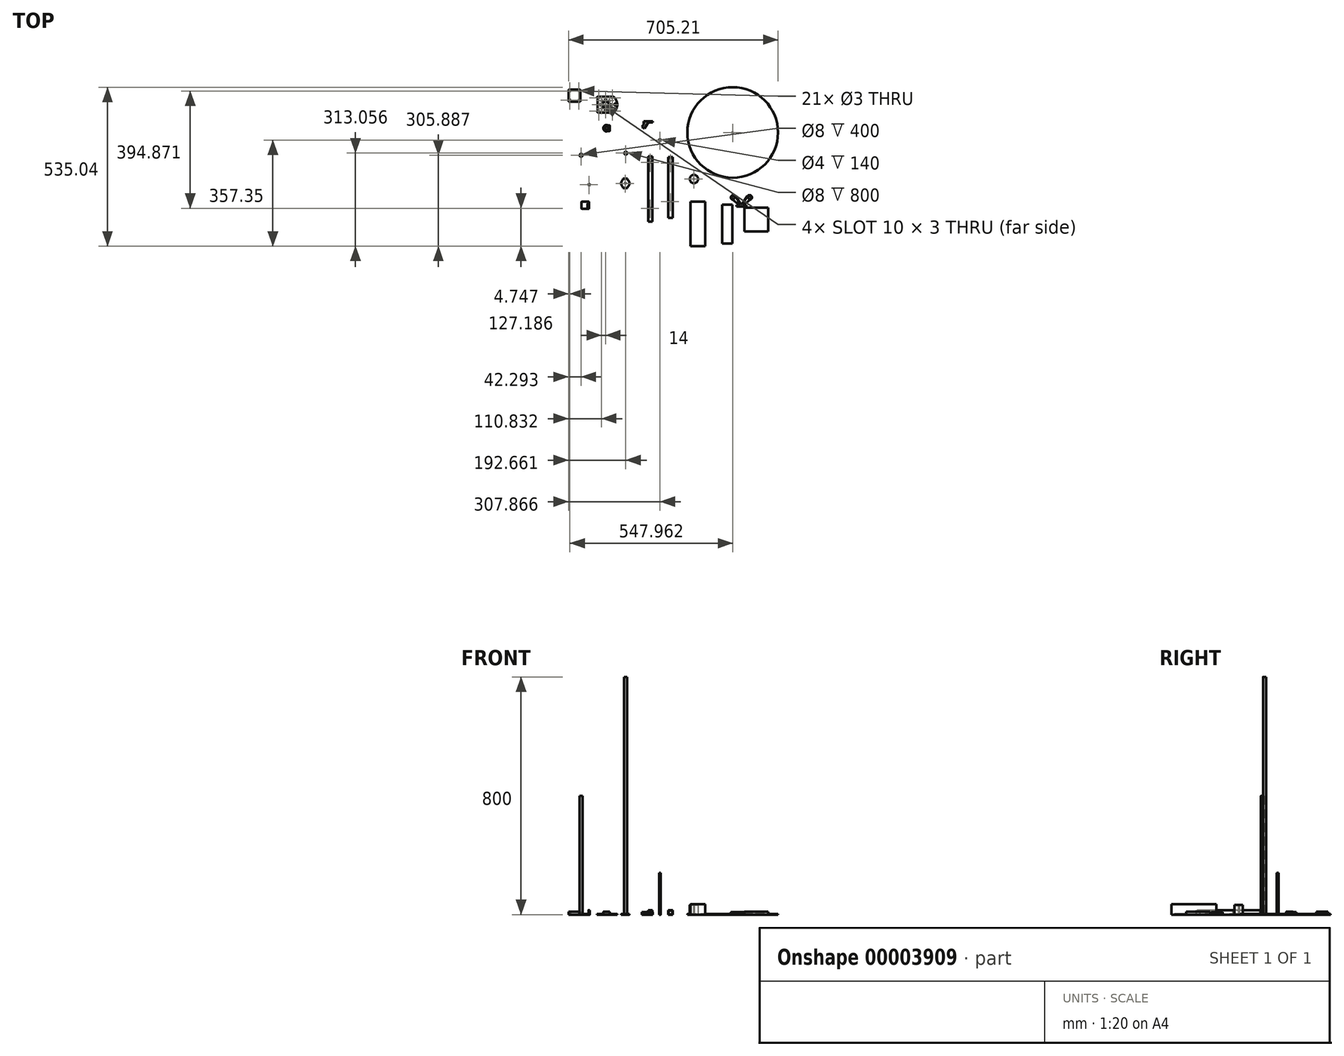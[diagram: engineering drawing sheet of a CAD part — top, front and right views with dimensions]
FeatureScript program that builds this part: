
annotation { "Feature Type Name" : "Feature", "Feature Type Description" : "" }
export const myFeature = defineFeature(function(context is Context, id is Id, definition is map)
    precondition{}
    {
        {
            var Q0;
            Q0=qCreatedBy(makeId("Top.planeOp"),FACE);
            var sketch = newSketch(context, id + "F0", { "sketchPlane" : qUnion([Q0])});
            skLineSegment(sketch, "E0.bottom", {"start": v(-54.12, 60.88) * mm, "end": v(-39.12, 60.88) * mm});
            skLineSegment(sketch, "E0.top", {"start": v(-54.12, -159.12) * mm, "end": v(-39.12, -159.12) * mm});
            skLineSegment(sketch, "E0.left", {"start": v(-54.12, 60.88) * mm, "end": v(-54.12, -159.12) * mm});
            skLineSegment(sketch, "E0.right", {"start": v(-39.12, 60.88) * mm, "end": v(-39.12, -159.12) * mm});
            skLineSegment(sketch, "E1", {"start": v(-54.12, -114.12) * mm, "end": v(-39.12, -114.12) * mm});
            skCircle(sketch, "E2", {"center": v(-46.62, -114.12) * mm, "radius": 1.5 * mm});
            skLineSegment(sketch, "E3", {"start": v(-54.12, 40.88) * mm, "end": v(-39.12, 40.88) * mm});
            skPoint(sketch, "E4", {"position": v(-46.62, 40.88) * mm});
            skCircle(sketch, "E5", {"center": v(-46.62, 40.88) * mm, "radius": 1.5 * mm});
            skSolve(sketch);
        }
        {
            var Q0;
            {var subQ8=sQuery(id+"F0.wireOp",EDGE,"E0.bottom");Q0=makeQuery(id+"F0.imprint","IMPRINT",FACE,{"disambiguationData":[TD([[makeQuery(id+"F0.imprint","IMPRINT",EDGE,{"derivedFrom":subQ8}),-1.0]])]});}
            var Q1;
            {var subQ8=sQuery(id+"F0.wireOp",EDGE,"E0.top");Q1=makeQuery(id+"F0.imprint","IMPRINT",FACE,{"disambiguationData":[TD([[makeQuery(id+"F0.imprint","IMPRINT",EDGE,{"derivedFrom":subQ8}),1.0]])]});}
            var Q2;
            {var subQ3=sQuery(id+"F0.wireOp",EDGE,"E0.left");var subQ6=sQuery(id+"F0.wireOp",EDGE,"E1");var subQ13=makeQuery(id+"F0.imprint","INTERSECT",VERTEX,{"derivedFrom":[subQ3,subQ6]});Q2=makeQuery(id+"F0.imprint","IMPRINT",FACE,{"disambiguationData":[TD([[makeQuery(id+"F0.imprint","IMPRINT",EDGE,{"disambiguationData":[TD([[subQ13,1.0]])],"derivedFrom":subQ3}),1.0]])]});}
            extrude(context, id + "F1", {"entities" : qUnion([Q0, Q1, Q2]), "depth" : 15 * mm});
        }
        {
            var Q0;
            Q0=qCreatedBy(makeId("Top.planeOp"),FACE);
            var sketch = newSketch(context, id + "F2", { "sketchPlane" : qUnion([Q0])});
            skLineSegment(sketch, "E6.bottom", {"start": v(13.47, 58.55) * mm, "end": v(28.47, 58.55) * mm});
            skLineSegment(sketch, "E6.top", {"start": v(13.47, -146.45) * mm, "end": v(28.47, -146.45) * mm});
            skLineSegment(sketch, "E6.left", {"start": v(13.47, 58.55) * mm, "end": v(13.47, -146.45) * mm});
            skLineSegment(sketch, "E6.right", {"start": v(28.47, 58.55) * mm, "end": v(28.47, -146.45) * mm});
            skLineSegment(sketch, "E7", {"start": v(13.47, -91.45) * mm, "end": v(28.47, -91.45) * mm});
            skCircle(sketch, "E8", {"center": v(20.97, -91.45) * mm, "radius": 1.5 * mm});
            skLineSegment(sketch, "E9", {"start": v(13.47, 38.55) * mm, "end": v(28.47, 38.55) * mm});
            skCircle(sketch, "E10", {"center": v(20.97, 38.55) * mm, "radius": 1.5 * mm});
            skSolve(sketch);
        }
        {
            var Q0;
            {var subQ7=sQuery(id+"F2.wireOp",EDGE,"E6.left");var subQ10=sQuery(id+"F2.wireOp",EDGE,"E6.bottom");var subQ12=sQuery(id+"F2.wireOp",EDGE,"E7");var subQ17=makeQuery(id+"F2.imprint","INTERSECT",VERTEX,{"derivedFrom":[subQ7,subQ12]});var subQ19=sQuery(id+"F2.wireOp",EDGE,"E6.top");Q0=qUnion([makeQuery(id+"F2.imprint","IMPRINT",FACE,{"disambiguationData":[TD([[makeQuery(id+"F2.imprint","IMPRINT",EDGE,{"derivedFrom":subQ10}),-1.0]])]}),makeQuery(id+"F2.imprint","IMPRINT",FACE,{"disambiguationData":[TD([[makeQuery(id+"F2.imprint","IMPRINT",EDGE,{"derivedFrom":subQ19}),1.0]])]}),makeQuery(id+"F2.imprint","IMPRINT",FACE,{"disambiguationData":[TD([[makeQuery(id+"F2.imprint","IMPRINT",EDGE,{"disambiguationData":[TD([[subQ17,1.0]])],"derivedFrom":subQ7}),1.0]])]})]);}
            extrude(context, id + "F3", {"entities" : qUnion([Q0]), "depth" : 15 * mm});
        }
        {
            var Q0;
            Q0=qCreatedBy(makeId("Top.planeOp"),FACE);
            var sketch = newSketch(context, id + "F4", { "sketchPlane" : qUnion([Q0])});
            skCircle(sketch, "E11", {"center": v(100.22, -15.34) * mm, "radius": 14 * mm});
            skCircle(sketch, "E12", {"center": v(100.22, -15.34) * mm, "radius": 1.5 * mm});
            skSolve(sketch);
        }
        {
            var Q0;
            Q0=makeQuery(id+"F4.imprint","IMPRINT",FACE,{"disambiguationData":[TD([[makeQuery(id+"F4.imprint","IMPRINT",EDGE,{"derivedFrom":sQuery(id+"F4.wireOp",EDGE,"E11")}),1.0]])]});
            extrude(context, id + "F5", {"entities" : qUnion([Q0]), "depth" : 32 * mm});
        }
        {
            var Q0;
            Q0=qCreatedBy(makeId("Top.planeOp"),FACE);
            var sketch = newSketch(context, id + "F6", { "sketchPlane" : qUnion([Q0])});
            skLineSegment(sketch, "E13.bottom", {"start": v(-138.25, -13.9) * mm, "end": v(-123.25, -13.9) * mm});
            skLineSegment(sketch, "E13.top", {"start": v(-138.25, -45.9) * mm, "end": v(-123.25, -45.9) * mm});
            skLineSegment(sketch, "E13.left", {"start": v(-138.25, -13.9) * mm, "end": v(-138.25, -45.9) * mm});
            skLineSegment(sketch, "E13.right", {"start": v(-123.25, -13.9) * mm, "end": v(-123.25, -45.9) * mm});
            skPoint(sketch, "E14", {"position": v(-123.25, -29.9) * mm});
            skLineSegment(sketch, "E15", {"start": v(-123.25, -29.9) * mm, "end": v(-138.25, -29.9) * mm});
            skCircle(sketch, "E16", {"center": v(-130.75, -29.9) * mm, "radius": 14 * mm});
            skCircle(sketch, "E17", {"center": v(-130.75, -29.9) * mm, "radius": 1.5 * mm});
            skSolve(sketch);
        }
        {
            var Q0;
            {var subQ1=sQuery(id+"F6.wireOp",EDGE,"E13.right");var subQ3=sQuery(id+"F6.wireOp",EDGE,"E13.left");var subQ6=sQuery(id+"F6.wireOp",EDGE,"E13.bottom");var subQ10=sQuery(id+"F6.wireOp",EDGE,"E13.top");var subQ11=sQuery(id+"F6.wireOp",EDGE,"E15");var subQ12=makeQuery(id+"F6.imprint","INTERSECT",VERTEX,{"derivedFrom":[subQ3,subQ11]});var subQ13=makeQuery(id+"F6.imprint","IMPRINT",EDGE,{"disambiguationData":[TD([[subQ12,-1.0]])],"derivedFrom":subQ3});var subQ14=makeQuery(id+"F6.imprint","IMPRINT",EDGE,{"disambiguationData":[TD([[subQ12,1.0]])],"derivedFrom":subQ3});var subQ15=makeQuery(id+"F6.imprint","INTERSECT",VERTEX,{"derivedFrom":[subQ1,subQ11]});var subQ17=makeQuery(id+"F6.imprint","IMPRINT",EDGE,{"disambiguationData":[TD([[subQ15,1.0]])],"derivedFrom":subQ1});Q0=qUnion([makeQuery(id+"F6.imprint","IMPRINT",FACE,{"disambiguationData":[TD([[makeQuery(id+"F6.imprint","IMPRINT",EDGE,{"derivedFrom":subQ6}),-1.0]])]}),makeQuery(id+"F6.imprint","IMPRINT",FACE,{"disambiguationData":[TD([[makeQuery(id+"F6.imprint","IMPRINT",EDGE,{"derivedFrom":subQ10}),1.0]])]}),makeQuery(id+"F6.imprint","IMPRINT",FACE,{"disambiguationData":[TD([[subQ14,-1.0]])]}),makeQuery(id+"F6.imprint","IMPRINT",FACE,{"disambiguationData":[TD([[subQ17,1.0]])]}),makeQuery(id+"F6.imprint","IMPRINT",FACE,{"disambiguationData":[TD([[subQ14,1.0]])]}),makeQuery(id+"F6.imprint","IMPRINT",FACE,{"disambiguationData":[TD([[subQ13,1.0]])]})]);}
            extrude(context, id + "F7", {"entities" : qUnion([Q0]), "depth" : 1.8 * mm});
        }
        {
            var Q0;
            Q0=qCreatedBy(makeId("Top.planeOp"),FACE);
            var sketch = newSketch(context, id + "F8", { "sketchPlane" : qUnion([Q0])});
            skCircle(sketch, "E18", {"center": v(-129.23, 71.75) * mm, "radius": 5 * mm});
            skCircle(sketch, "E19", {"center": v(-129.23, 71.75) * mm, "radius": 4 * mm});
            skSolve(sketch);
        }
        {
            var Q0;
            Q0=makeQuery(id+"F8.imprint","IMPRINT",FACE,{"disambiguationData":[TD([[makeQuery(id+"F8.imprint","IMPRINT",EDGE,{"derivedFrom":sQuery(id+"F8.wireOp",EDGE,"E18")}),1.0]])]});
            extrude(context, id + "F9", {"entities" : qUnion([Q0]), "depth" : 800 * mm});
        }
        {
            var Q0;
            Q0=qCreatedBy(makeId("Top.planeOp"),FACE);
            var sketch = newSketch(context, id + "F10", { "sketchPlane" : qUnion([Q0])});
            skCircle(sketch, "E20", {"center": v(230.82, 141.23) * mm, "radius": 1.5 * mm});
            skCircle(sketch, "E21", {"center": v(230.82, 141.23) * mm, "radius": 152.5 * mm});
            skSolve(sketch);
        }
        {
            var Q0;
            Q0=makeQuery(id+"F10.imprint","IMPRINT",FACE,{"disambiguationData":[TD([[makeQuery(id+"F10.imprint","IMPRINT",EDGE,{"derivedFrom":sQuery(id+"F10.wireOp",EDGE,"E20")}),-1.0]])]});
            extrude(context, id + "F11", {"entities" : qUnion([Q0]), "depth" : 2 * mm});
        }
        {
            var Q0;
            Q0=qCreatedBy(makeId("Top.planeOp"),FACE);
            var sketch = newSketch(context, id + "F12", { "sketchPlane" : qUnion([Q0])});
            skLineSegment(sketch, "E22", {"start": v(-182.66, 164.93) * mm, "end": v(-182.66, 146.73) * mm});
            skCircle(sketch, "E23", {"center": v(-193.66, 155.76) * mm, "radius": 11 * mm});
            skPoint(sketch, "E24", {"position": v(-182.66, 155.83) * mm});
            skLineSegment(sketch, "E25", {"start": v(-182.66, 164.93) * mm, "end": v(-193.13, 166.75) * mm});
            skLineSegment(sketch, "E26", {"start": v(-193.13, 144.78) * mm, "end": v(-182.66, 146.73) * mm});
            skCircle(sketch, "E27", {"center": v(-193.66, 155.76) * mm, "radius": 5 * mm});
            skSolve(sketch);
        }
        {
            var Q0;
            {var subQ0=sQuery(id+"F12.wireOp",EDGE,"E25");var subQ1=sQuery(id+"F12.wireOp",EDGE,"E23");var subQ3=sQuery(id+"F12.wireOp",EDGE,"E22");var subQ4=makeQuery(id+"F12.imprint","INTERSECT",VERTEX,{"derivedFrom":[subQ3,subQ0]});var subQ5=makeQuery(id+"F12.imprint","INTERSECT",VERTEX,{"disambiguationData":[OD(0.0)],"derivedFrom":[subQ3,subQ1]});var subQ8=makeQuery(id+"F12.imprint","IMPRINT",EDGE,{"disambiguationData":[TD([[subQ5,-1.0]])],"derivedFrom":subQ3});var subQ9=sQuery(id+"F12.wireOp",EDGE,"E26");var subQ12=makeQuery(id+"F12.imprint","INTERSECT",VERTEX,{"derivedFrom":[subQ3,subQ9]});var subQ13=makeQuery(id+"F12.imprint","INTERSECT",VERTEX,{"disambiguationData":[OD(0.0)],"derivedFrom":[subQ1,subQ0]});var subQ15=makeQuery(id+"F12.imprint","INTERSECT",VERTEX,{"disambiguationData":[OD(0.0)],"derivedFrom":[subQ1,subQ9]});Q0=qUnion([makeQuery(id+"F12.imprint","IMPRINT",FACE,{"disambiguationData":[TD([[makeQuery(id+"F12.imprint","IMPRINT",EDGE,{"disambiguationData":[TD([[subQ4,-1.0]])],"derivedFrom":subQ3}),-1.0]])]}),makeQuery(id+"F12.imprint","IMPRINT",FACE,{"disambiguationData":[TD([[subQ8,1.0]])]}),makeQuery(id+"F12.imprint","IMPRINT",FACE,{"disambiguationData":[TD([[makeQuery(id+"F12.imprint","IMPRINT",EDGE,{"disambiguationData":[TD([[subQ12,1.0]])],"derivedFrom":subQ3}),-1.0]])]}),makeQuery(id+"F12.imprint","IMPRINT",FACE,{"disambiguationData":[TD([[makeQuery(id+"F12.imprint","IMPRINT",EDGE,{"disambiguationData":[TD([[subQ13,1.0]])],"derivedFrom":subQ1}),1.0]])]}),makeQuery(id+"F12.imprint","IMPRINT",FACE,{"disambiguationData":[TD([[makeQuery(id+"F12.imprint","IMPRINT",EDGE,{"disambiguationData":[TD([[subQ15,-1.0]])],"derivedFrom":subQ1}),1.0]])]}),makeQuery(id+"F12.imprint","IMPRINT",FACE,{"disambiguationData":[TD([[makeQuery(id+"F12.imprint","IMPRINT",EDGE,{"derivedFrom":sQuery(id+"F12.wireOp",EDGE,"E27")}),-1.0]])]})]);}
            extrude(context, id + "F13", {"entities" : qUnion([Q0]), "depth" : 10 * mm});
        }
        {
            var Q0;
            {var subQ0=sQuery(id+"F12.wireOp",EDGE,"E22");Q0=makeQuery(id+"F13.opExtrude","SWEPT_FACE",FACE,{"disambiguationData":[OSD([subQ0]),TDD([makeQuery(id+"F12.imprint","IMPRINT",EDGE,{"disambiguationData":[TD([[makeQuery(id+"F12.imprint","INTERSECT",VERTEX,{"derivedFrom":[subQ0,sQuery(id+"F12.wireOp",EDGE,"E25")]}),-1.0]])],"derivedFrom":subQ0})])]});}
            var sketch = newSketch(context, id + "F14", { "sketchPlane" : qUnion([Q0])});
            skPoint(sketch, "E28", {"position": v(146.73, 5) * mm});
            skCircle(sketch, "E29", {"center": v(149.73, 5) * mm, "radius": 1.25 * mm});
            skCircle(sketch, "E30", {"center": v(161.93, 5) * mm, "radius": 1.25 * mm});
            skSolve(sketch);
        }
        {
            var Q0;
            {Q0=qUnion([makeQuery(id+"F14.imprint","IMPRINT",FACE,{"disambiguationData":[TD([[makeQuery(id+"F14.imprint","IMPRINT",EDGE,{"derivedFrom":sQuery(id+"F14.wireOp",EDGE,"E29")}),1.0]])]}),makeQuery(id+"F14.imprint","IMPRINT",FACE,{"disambiguationData":[TD([[makeQuery(id+"F14.imprint","IMPRINT",EDGE,{"derivedFrom":sQuery(id+"F14.wireOp",EDGE,"E30")}),1.0]])]})]);}
            extrude(context, id + "F15", {"entities" : qUnion([Q0]), "operationType" : NewBodyOperationType.REMOVE, "oppositeDirection" : true, "depth" : 10 * mm});
        }
        {
            var Q0;
            Q0=makeQuery(id+"F13.opExtrude","SWEPT_FACE",FACE,{"disambiguationData":[OSD([sQuery(id+"F12.wireOp",EDGE,"E26")])]});
            var Q1;
            {var subQ0=sQuery(id+"F12.wireOp",EDGE,"E23");var subQ1=sQuery(id+"F12.wireOp",EDGE,"E25");var subQ2=makeQuery(id+"F12.imprint","INTERSECT",VERTEX,{"disambiguationData":[OD(0.0)],"derivedFrom":[subQ0,subQ1]});var subQ3=sQuery(id+"F12.wireOp",EDGE,"E26");var subQ4=makeQuery(id+"F12.imprint","INTERSECT",VERTEX,{"disambiguationData":[OD(0.0)],"derivedFrom":[subQ0,subQ3]});Q1=makeQuery(id+"F13.opExtrude","SWEPT_FACE",FACE,{"disambiguationData":[OSD([subQ0]),TDD([makeQuery(id+"F12.imprint","IMPRINT",EDGE,{"disambiguationData":[TD([[subQ2,1.0]])],"derivedFrom":subQ0}),makeQuery(id+"F12.imprint","IMPRINT",EDGE,{"disambiguationData":[TD([[subQ2,-1.0]])],"derivedFrom":subQ0}),makeQuery(id+"F12.imprint","IMPRINT",EDGE,{"disambiguationData":[TD([[subQ4,-1.0]])],"derivedFrom":subQ0})])]});}
            var Q2;
            Q2=makeQuery(id+"F13.opExtrude","SWEPT_FACE",FACE,{"disambiguationData":[OSD([sQuery(id+"F12.wireOp",EDGE,"E25")])]});
            fillet(context, id + "F16", {"entities" : qUnion([Q0, Q1, Q2]), "radius" : 1 * mm, "tangentPropagation" : true, "allowEdgeOverflow" : false});
        }
        {
            var Q0;
            Q0=qCreatedBy(makeId("Top.planeOp"),FACE);
            var sketch = newSketch(context, id + "F17", { "sketchPlane" : qUnion([Q0])});
            skCircle(sketch, "E31", {"center": v(-279.6, 64.58) * mm, "radius": 5 * mm});
            skCircle(sketch, "E32", {"center": v(-279.6, 64.58) * mm, "radius": 4 * mm});
            skSolve(sketch);
        }
        {
            var Q0;
            Q0=makeQuery(id+"F17.imprint","IMPRINT",FACE,{"disambiguationData":[TD([[makeQuery(id+"F17.imprint","IMPRINT",EDGE,{"derivedFrom":sQuery(id+"F17.wireOp",EDGE,"E31")}),1.0]])]});
            extrude(context, id + "F18", {"entities" : qUnion([Q0]), "depth" : 400 * mm});
        }
        {
            var Q0;
            Q0=qCreatedBy(makeId("Top.planeOp"),FACE);
            var sketch = newSketch(context, id + "F19", { "sketchPlane" : qUnion([Q0])});
            skLineSegment(sketch, "E33", {"start": v(-37.82, 178.67) * mm, "end": v(-69.22, 178.67) * mm});
            skLineSegment(sketch, "E34", {"start": v(-37.82, 178.67) * mm, "end": v(-37.82, 175.67) * mm});
            skLineSegment(sketch, "E35", {"start": v(-37.82, 175.67) * mm, "end": v(-53.82, 175.67) * mm});
            skLineSegment(sketch, "E36", {"start": v(-53.82, 175.67) * mm, "end": v(-66.07, 154.45) * mm});
            skLineSegment(sketch, "E37", {"start": v(-66.07, 154.45) * mm, "end": v(-74.73, 159.45) * mm});
            skLineSegment(sketch, "E38", {"start": v(-74.73, 159.45) * mm, "end": v(-69.22, 169) * mm});
            skLineSegment(sketch, "E39", {"start": v(-69.22, 178.67) * mm, "end": v(-69.22, 169) * mm});
            skSolve(sketch);
        }
        {
            var Q0;
            Q0=makeQuery(id+"F19.imprint","IMPRINT",FACE,{"disambiguationData":[TD([[makeQuery(id+"F19.imprint","IMPRINT",EDGE,{"derivedFrom":sQuery(id+"F19.wireOp",EDGE,"E33")}),1.0]])]});
            extrude(context, id + "F20", {"entities" : qUnion([Q0]), "depth" : 7.9 * mm});
        }
        {
            var Q0;
            Q0=makeQuery(id+"F20.opExtrude","SWEPT_FACE",FACE,{"disambiguationData":[OSD([sQuery(id+"F19.wireOp",EDGE,"E37")])]});
            var sketch = newSketch(context, id + "F21", { "sketchPlane" : qUnion([Q0])});
            skPoint(sketch, "E40", {"position": v(-144.44, 3.95) * mm});
            skCircle(sketch, "E41", {"center": v(-139.94, 3.95) * mm, "radius": 3 * mm});
            skSolve(sketch);
        }
        {
            var Q0;
            Q0=makeQuery(id+"F21.imprint","IMPRINT",FACE,{"disambiguationData":[TD([[makeQuery(id+"F21.imprint","IMPRINT",EDGE,{"derivedFrom":sQuery(id+"F21.wireOp",EDGE,"E41")}),1.0]])]});
            extrude(context, id + "F22", {"entities" : qUnion([Q0]), "operationType" : NewBodyOperationType.REMOVE, "oppositeDirection" : true, "depth" : 27 * mm});
        }
        {
            var Q0;
            Q0=makeQuery(id+"F20.opExtrude","SWEPT_FACE",FACE,{"disambiguationData":[OSD([sQuery(id+"F19.wireOp",EDGE,"E33")])]});
            var sketch = newSketch(context, id + "F23", { "sketchPlane" : qUnion([Q0])});
            skPoint(sketch, "E42", {"position": v(69.22, 3.95) * mm});
            skCircle(sketch, "E43", {"center": v(64.57, 3.95) * mm, "radius": 1.5 * mm});
            skCircle(sketch, "E44", {"center": v(44.57, 3.95) * mm, "radius": 1.5 * mm});
            skSolve(sketch);
        }
        {
            var Q0;
            {Q0=qUnion([makeQuery(id+"F23.imprint","IMPRINT",FACE,{"disambiguationData":[TD([[makeQuery(id+"F23.imprint","IMPRINT",EDGE,{"derivedFrom":sQuery(id+"F23.wireOp",EDGE,"E43")}),1.0]])]}),makeQuery(id+"F23.imprint","IMPRINT",FACE,{"disambiguationData":[TD([[makeQuery(id+"F23.imprint","IMPRINT",EDGE,{"derivedFrom":sQuery(id+"F23.wireOp",EDGE,"E44")}),1.0]])]})]);}
            extrude(context, id + "F24", {"entities" : qUnion([Q0]), "operationType" : NewBodyOperationType.REMOVE, "oppositeDirection" : true, "depth" : 5 * mm});
        }
        {
            var Q0;
            Q0=qCreatedBy(makeId("Top.planeOp"),FACE);
            var sketch = newSketch(context, id + "F25", { "sketchPlane" : qUnion([Q0])});
            skCircle(sketch, "E45", {"center": v(-14.02, 116.04) * mm, "radius": 3 * mm});
            skCircle(sketch, "E46", {"center": v(-14.02, 116.04) * mm, "radius": 2 * mm});
            skSolve(sketch);
        }
        {
            var Q0;
            Q0=makeQuery(id+"F25.imprint","IMPRINT",FACE,{"disambiguationData":[TD([[makeQuery(id+"F25.imprint","IMPRINT",EDGE,{"derivedFrom":sQuery(id+"F25.wireOp",EDGE,"E45")}),1.0]])]});
            extrude(context, id + "F26", {"entities" : qUnion([Q0]), "depth" : 140 * mm});
        }
        {
            var Q0;
            Q0=qCreatedBy(makeId("Top.planeOp"),FACE);
            var sketch = newSketch(context, id + "F27", { "sketchPlane" : qUnion([Q0])});
            skCircle(sketch, "E47", {"center": v(232.6, -77.35) * mm, "radius": 5 * mm});
            skCircle(sketch, "E48", {"center": v(287.6, -77.35) * mm, "radius": 5 * mm});
            skCircle(sketch, "E49", {"center": v(287.6, -77.35) * mm, "radius": 8 * mm});
            skCircle(sketch, "E50", {"center": v(232.6, -77.35) * mm, "radius": 8 * mm});
            skPoint(sketch, "E51", {"position": v(260.1, -107.85) * mm});
            skPoint(sketch, "E52", {"position": v(260.1, -101.95) * mm});
            skLineSegment(sketch, "E53", {"start": v(276.1, -107.85) * mm, "end": v(244.1, -107.85) * mm});
            skLineSegment(sketch, "E54", {"start": v(261.6, -101.95) * mm, "end": v(258.6, -101.95) * mm});
            skLineSegment(sketch, "E55", {"start": v(261.6, -101.95) * mm, "end": v(280.94, -72.91) * mm});
            skLineSegment(sketch, "E56", {"start": v(258.6, -101.95) * mm, "end": v(239.26, -72.91) * mm});
            skPoint(sketch, "E57", {"position": v(287.6, -85.35) * mm});
            skPoint(sketch, "E58", {"position": v(232.6, -85.35) * mm});
            skLineSegment(sketch, "E59", {"start": v(244.1, -107.85) * mm, "end": v(244.1, -103.55) * mm});
            skLineSegment(sketch, "E60", {"start": v(244.1, -103.55) * mm, "end": v(276.1, -103.55) * mm});
            skLineSegment(sketch, "E61", {"start": v(276.1, -103.55) * mm, "end": v(276.1, -107.85) * mm});
            skPoint(sketch, "E62", {"position": v(248.95, -103.55) * mm});
            skPoint(sketch, "E63", {"position": v(271.25, -103.55) * mm});
            skPoint(sketch, "E64", {"position": v(271.25, -100.05) * mm});
            skPoint(sketch, "E65", {"position": v(248.95, -100.05) * mm});
            skLineSegment(sketch, "E66", {"start": v(232.6, -85.35) * mm, "end": v(248.95, -100.05) * mm});
            skLineSegment(sketch, "E67", {"start": v(248.95, -100.05) * mm, "end": v(248.95, -103.55) * mm});
            skLineSegment(sketch, "E68", {"start": v(271.25, -103.55) * mm, "end": v(271.25, -100.05) * mm});
            skLineSegment(sketch, "E69", {"start": v(271.25, -100.05) * mm, "end": v(287.6, -85.35) * mm});
            skSolve(sketch);
        }
        {
            var Q0;
            {Q0=qUnion([makeQuery(id+"F27.imprint","IMPRINT",FACE,{"disambiguationData":[TD([[makeQuery(id+"F27.imprint","IMPRINT",EDGE,{"derivedFrom":sQuery(id+"F27.wireOp",EDGE,"E53")}),-1.0]])]}),makeQuery(id+"F27.imprint","IMPRINT",FACE,{"disambiguationData":[TD([[makeQuery(id+"F27.imprint","IMPRINT",EDGE,{"derivedFrom":sQuery(id+"F27.wireOp",EDGE,"E47")}),-1.0]])]}),makeQuery(id+"F27.imprint","IMPRINT",FACE,{"disambiguationData":[TD([[makeQuery(id+"F27.imprint","IMPRINT",EDGE,{"derivedFrom":sQuery(id+"F27.wireOp",EDGE,"E48")}),-1.0]])]}),makeQuery(id+"F27.imprint","IMPRINT",FACE,{"disambiguationData":[TD([[makeQuery(id+"F27.imprint","IMPRINT",EDGE,{"derivedFrom":sQuery(id+"F27.wireOp",EDGE,"E54")}),1.0]])]})]);}
            extrude(context, id + "F28", {"entities" : qUnion([Q0]), "depth" : 8.1 * mm});
        }
        {
            var Q0;
            Q0=qCreatedBy(makeId("Top.planeOp"),FACE);
            var sketch = newSketch(context, id + "F29", { "sketchPlane" : qUnion([Q0])});
            skLineSegment(sketch, "E70.bottom", {"start": v(195.15, -101.92) * mm, "end": v(230.15, -101.92) * mm});
            skLineSegment(sketch, "E70.top", {"start": v(195.15, -231.92) * mm, "end": v(230.15, -231.92) * mm});
            skLineSegment(sketch, "E70.left", {"start": v(195.15, -101.92) * mm, "end": v(195.15, -231.92) * mm});
            skLineSegment(sketch, "E70.right", {"start": v(230.15, -101.92) * mm, "end": v(230.15, -231.92) * mm});
            skSolve(sketch);
        }
        {
            var Q0;
            Q0=makeQuery(id+"F29.imprint","IMPRINT",FACE,{"disambiguationData":[TD([[makeQuery(id+"F29.imprint","IMPRINT",EDGE,{"derivedFrom":sQuery(id+"F29.wireOp",EDGE,"E70.bottom")}),-1.0]])]});
            extrude(context, id + "F30", {"entities" : qUnion([Q0]), "depth" : 1 * mm});
        }
        {
            var Q0;
            Q0=qCreatedBy(makeId("Top.planeOp"),FACE);
            var sketch = newSketch(context, id + "F31", { "sketchPlane" : qUnion([Q0])});
            skLineSegment(sketch, "E71.bottom", {"start": v(270.64, -112.24) * mm, "end": v(350.64, -112.24) * mm});
            skLineSegment(sketch, "E71.top", {"start": v(270.64, -192.24) * mm, "end": v(350.64, -192.24) * mm});
            skLineSegment(sketch, "E71.left", {"start": v(270.64, -112.24) * mm, "end": v(270.64, -192.24) * mm});
            skLineSegment(sketch, "E71.right", {"start": v(350.64, -112.24) * mm, "end": v(350.64, -192.24) * mm});
            skSolve(sketch);
        }
        {
            var Q0;
            Q0=makeQuery(id+"F31.imprint","IMPRINT",FACE,{"disambiguationData":[TD([[makeQuery(id+"F31.imprint","IMPRINT",EDGE,{"derivedFrom":sQuery(id+"F31.wireOp",EDGE,"E71.bottom")}),-1.0]])]});
            extrude(context, id + "F32", {"entities" : qUnion([Q0]), "depth" : 10 * mm});
        }
        {
            var Q0;
            Q0=qCreatedBy(makeId("Top.planeOp"),FACE);
            var sketch = newSketch(context, id + "F33", { "sketchPlane" : qUnion([Q0])});
            skLineSegment(sketch, "E72.bottom", {"start": v(88.23, -91.3) * mm, "end": v(138.23, -91.3) * mm});
            skLineSegment(sketch, "E72.top", {"start": v(88.23, -241.3) * mm, "end": v(138.23, -241.3) * mm});
            skLineSegment(sketch, "E72.left", {"start": v(88.23, -91.3) * mm, "end": v(88.23, -241.3) * mm});
            skLineSegment(sketch, "E72.right", {"start": v(138.23, -91.3) * mm, "end": v(138.23, -241.3) * mm});
            skSolve(sketch);
        }
        {
            var Q0;
            Q0=makeQuery(id+"F33.imprint","IMPRINT",FACE,{"disambiguationData":[TD([[makeQuery(id+"F33.imprint","IMPRINT",EDGE,{"derivedFrom":sQuery(id+"F33.wireOp",EDGE,"E72.bottom")}),-1.0]])]});
            extrude(context, id + "F34", {"entities" : qUnion([Q0]), "depth" : 35 * mm});
        }
        {
            var Q0;
            Q0=qCreatedBy(makeId("Top.planeOp"),FACE);
            var sketch = newSketch(context, id + "F35", { "sketchPlane" : qUnion([Q0])});
            skCircle(sketch, "E73", {"center": v(-252.35, -34.13) * mm, "radius": 1.5 * mm});
            skCircle(sketch, "E74", {"center": v(-252.35, -34.13) * mm, "radius": 2.5 * mm});
            skSolve(sketch);
        }
        {
            var Q0;
            Q0=makeQuery(id+"F35.imprint","IMPRINT",FACE,{"disambiguationData":[TD([[makeQuery(id+"F35.imprint","IMPRINT",EDGE,{"derivedFrom":sQuery(id+"F35.wireOp",EDGE,"E73")}),-1.0]])]});
            extrude(context, id + "F36", {"entities" : qUnion([Q0]), "depth" : 15 * mm});
        }
        {
            var Q0;
            Q0=makeQuery(id+"F3.opExtrude","SWEPT_FACE",FACE,{"disambiguationData":[OSD([sQuery(id+"F2.wireOp",EDGE,"E6.right")])]});
            var sketch = newSketch(context, id + "F37", { "sketchPlane" : qUnion([Q0])});
            skPoint(sketch, "E75", {"position": v(-146.45, 7.5) * mm});
            skCircle(sketch, "E76", {"center": v(-106.45, 7.5) * mm, "radius": 4 * mm});
            skSolve(sketch);
        }
        {
            var Q0;
            Q0=makeQuery(id+"F37.imprint","IMPRINT",FACE,{"disambiguationData":[TD([[makeQuery(id+"F37.imprint","IMPRINT",EDGE,{"derivedFrom":sQuery(id+"F37.wireOp",EDGE,"E76")}),1.0]])]});
            extrude(context, id + "F38", {"entities" : qUnion([Q0]), "operationType" : NewBodyOperationType.REMOVE, "oppositeDirection" : true, "depth" : 15 * mm});
        }
        {
            var Q0;
            Q0=makeQuery(id+"F3.opExtrude","SWEPT_FACE",FACE,{"disambiguationData":[OSD([sQuery(id+"F2.wireOp",EDGE,"E6.top")])]});
            var sketch = newSketch(context, id + "F39", { "sketchPlane" : qUnion([Q0])});
            skLineSegment(sketch, "E77.bottom", {"start": v(14.47, 14) * mm, "end": v(27.47, 14) * mm});
            skLineSegment(sketch, "E77.top", {"start": v(14.47, 1) * mm, "end": v(27.47, 1) * mm});
            skLineSegment(sketch, "E77.left", {"start": v(14.47, 14) * mm, "end": v(14.47, 1) * mm});
            skLineSegment(sketch, "E77.right", {"start": v(27.47, 14) * mm, "end": v(27.47, 1) * mm});
            skSolve(sketch);
        }
        {
            var Q0;
            Q0=makeQuery(id+"F39.imprint","IMPRINT",FACE,{"disambiguationData":[TD([[makeQuery(id+"F39.imprint","IMPRINT",EDGE,{"derivedFrom":sQuery(id+"F39.wireOp",EDGE,"E77.bottom")}),-1.0]])]});
            extrude(context, id + "F40", {"entities" : qUnion([Q0]), "operationType" : NewBodyOperationType.REMOVE, "oppositeDirection" : true, "depth" : 200 * mm});
        }
        {
            var Q0;
            Q0=makeQuery(id+"F1.opExtrude","SWEPT_FACE",FACE,{"disambiguationData":[OSD([sQuery(id+"F0.wireOp",EDGE,"E0.top")])]});
            var sketch = newSketch(context, id + "F41", { "sketchPlane" : qUnion([Q0])});
            skLineSegment(sketch, "E78.bottom", {"start": v(-53.12, 14) * mm, "end": v(-40.12, 14) * mm});
            skLineSegment(sketch, "E78.top", {"start": v(-53.12, 1) * mm, "end": v(-40.12, 1) * mm});
            skLineSegment(sketch, "E78.left", {"start": v(-53.12, 14) * mm, "end": v(-53.12, 1) * mm});
            skLineSegment(sketch, "E78.right", {"start": v(-40.12, 14) * mm, "end": v(-40.12, 1) * mm});
            skSolve(sketch);
        }
        {
            var Q0;
            Q0=makeQuery(id+"F41.imprint","IMPRINT",FACE,{"disambiguationData":[TD([[makeQuery(id+"F41.imprint","IMPRINT",EDGE,{"derivedFrom":sQuery(id+"F41.wireOp",EDGE,"E78.bottom")}),-1.0]])]});
            extrude(context, id + "F42", {"entities" : qUnion([Q0]), "operationType" : NewBodyOperationType.REMOVE, "oppositeDirection" : true, "depth" : 220 * mm});
        }
        {
            var Q0;
            Q0=makeQuery(id+"F1.opExtrude","SWEPT_FACE",FACE,{"disambiguationData":[OSD([sQuery(id+"F0.wireOp",EDGE,"E0.right")])]});
            var sketch = newSketch(context, id + "F43", { "sketchPlane" : qUnion([Q0])});
            skPoint(sketch, "E79", {"position": v(-159.12, 7.5) * mm});
            skCircle(sketch, "E80", {"center": v(-124.12, 7.5) * mm, "radius": 4.16 * mm});
            skSolve(sketch);
        }
        {
            var Q0;
            Q0=makeQuery(id+"F43.imprint","IMPRINT",FACE,{"disambiguationData":[TD([[makeQuery(id+"F43.imprint","IMPRINT",EDGE,{"derivedFrom":sQuery(id+"F43.wireOp",EDGE,"E80")}),1.0]])]});
            extrude(context, id + "F44", {"entities" : qUnion([Q0]), "operationType" : NewBodyOperationType.REMOVE, "oppositeDirection" : true, "depth" : 15 * mm});
        }
        {
            var Q0;
            Q0=qCreatedBy(makeId("Top.planeOp"),FACE);
            var sketch = newSketch(context, id + "F45", { "sketchPlane" : qUnion([Q0])});
            skLineSegment(sketch, "E81.bottom", {"start": v(-275.96, -91.26) * mm, "end": v(-254.96, -91.26) * mm});
            skLineSegment(sketch, "E81.top", {"start": v(-275.96, -116.06) * mm, "end": v(-254.96, -116.06) * mm});
            skLineSegment(sketch, "E81.left", {"start": v(-277.96, -93.26) * mm, "end": v(-277.96, -114.06) * mm});
            skLineSegment(sketch, "E81.right", {"start": v(-252.96, -93.26) * mm, "end": v(-252.96, -114.06) * mm});
            skPoint(sketch, "E82.visualSharp", {"position": v(-277.96, -91.26) * mm});
            skArc(sketch, "E82.filletArc", {"start": v(-275.96, -91.26) * mm, "mid": v(-277.37, -91.85) * mm, "end": v(-277.96, -93.26) * mm});
            skPoint(sketch, "E83.visualSharp", {"position": v(-277.96, -116.06) * mm});
            skArc(sketch, "E83.filletArc", {"start": v(-277.96, -114.06) * mm, "mid": v(-277.37, -115.48) * mm, "end": v(-275.96, -116.06) * mm});
            skPoint(sketch, "E84.visualSharp", {"position": v(-252.96, -116.06) * mm});
            skArc(sketch, "E84.filletArc", {"start": v(-254.96, -116.06) * mm, "mid": v(-253.54, -115.48) * mm, "end": v(-252.96, -114.06) * mm});
            skPoint(sketch, "E85.visualSharp", {"position": v(-252.96, -91.26) * mm});
            skArc(sketch, "E85.filletArc", {"start": v(-252.96, -93.26) * mm, "mid": v(-253.54, -91.85) * mm, "end": v(-254.96, -91.26) * mm});
            skLineSegment(sketch, "E86.bottom", {"start": v(-256.96, -97.26) * mm, "end": v(-256.96, -97.26) * mm});
            skLineSegment(sketch, "E86.top", {"start": v(-256.96, -110.06) * mm, "end": v(-256.96, -110.06) * mm});
            skLineSegment(sketch, "E86.left", {"start": v(-255.96, -98.26) * mm, "end": v(-255.96, -109.06) * mm});
            skLineSegment(sketch, "E86.right", {"start": v(-257.96, -98.26) * mm, "end": v(-257.96, -109.06) * mm});
            skPoint(sketch, "E87.visualSharp", {"position": v(-257.96, -97.26) * mm});
            skArc(sketch, "E87.filletArc", {"start": v(-256.96, -97.26) * mm, "mid": v(-257.66, -97.55) * mm, "end": v(-257.96, -98.26) * mm});
            skPoint(sketch, "E88.visualSharp", {"position": v(-255.96, -97.26) * mm});
            skArc(sketch, "E88.filletArc", {"start": v(-255.96, -98.26) * mm, "mid": v(-256.25, -97.55) * mm, "end": v(-256.96, -97.26) * mm});
            skPoint(sketch, "E89.visualSharp", {"position": v(-255.96, -110.06) * mm});
            skArc(sketch, "E89.filletArc", {"start": v(-256.96, -110.06) * mm, "mid": v(-256.25, -109.77) * mm, "end": v(-255.96, -109.06) * mm});
            skPoint(sketch, "E90.visualSharp", {"position": v(-257.96, -110.06) * mm});
            skArc(sketch, "E90.filletArc", {"start": v(-257.96, -109.06) * mm, "mid": v(-257.66, -109.77) * mm, "end": v(-256.96, -110.06) * mm});
            skSolve(sketch);
        }
        {
            var Q0;
            Q0=makeQuery(id+"F45.imprint","IMPRINT",FACE,{"disambiguationData":[TD([[makeQuery(id+"F45.imprint","IMPRINT",EDGE,{"derivedFrom":sQuery(id+"F45.wireOp",EDGE,"E81.bottom")}),-1.0]])]});
            extrude(context, id + "F46", {"entities" : qUnion([Q0]), "depth" : 1.8 * mm});
        }
        {
            var Q0;
            Q0=qCreatedBy(makeId("Top.planeOp"),FACE);
            var sketch = newSketch(context, id + "F47", { "sketchPlane" : qUnion([Q0])});
            skLineSegment(sketch, "E91.bottom", {"start": v(-321.9, 285.5) * mm, "end": v(-281.9, 285.5) * mm});
            skLineSegment(sketch, "E91.top", {"start": v(-321.9, 245.5) * mm, "end": v(-281.9, 245.5) * mm});
            skLineSegment(sketch, "E91.left", {"start": v(-321.9, 285.5) * mm, "end": v(-321.9, 245.5) * mm});
            skLineSegment(sketch, "E91.right", {"start": v(-281.9, 285.5) * mm, "end": v(-281.9, 245.5) * mm});
            skCircle(sketch, "E92", {"center": v(-317.14, 280.75) * mm, "radius": 1.5 * mm});
            skCircle(sketch, "E93", {"center": v(-286.64, 280.75) * mm, "radius": 1.5 * mm});
            skCircle(sketch, "E94", {"center": v(-286.64, 250.25) * mm, "radius": 1.5 * mm});
            skCircle(sketch, "E95", {"center": v(-317.14, 250.25) * mm, "radius": 1.5 * mm});
            skSolve(sketch);
        }
        {
            var Q0;
            Q0=makeQuery(id+"F47.imprint","IMPRINT",FACE,{"disambiguationData":[TD([[makeQuery(id+"F47.imprint","IMPRINT",EDGE,{"derivedFrom":sQuery(id+"F47.wireOp",EDGE,"E91.bottom")}),-1.0]])]});
            extrude(context, id + "F48", {"entities" : qUnion([Q0]), "depth" : 10 * mm});
        }
        {
            var Q0;
            Q0=qCreatedBy(makeId("Top.planeOp"),FACE);
            var sketch = newSketch(context, id + "F49", { "sketchPlane" : qUnion([Q0])});
            skLineSegment(sketch, "E96.bottom", {"start": v(-220.86, 261.77) * mm, "end": v(-173.25, 261.77) * mm});
            skLineSegment(sketch, "E96.top", {"start": v(-220.86, 208.77) * mm, "end": v(-173.25, 208.77) * mm});
            skLineSegment(sketch, "E96.left", {"start": v(-223.56, 261.77) * mm, "end": v(-223.56, 208.77) * mm});
            skCircle(sketch, "E97", {"center": v(-219.56, 257.77) * mm, "radius": 1.5 * mm});
            skCircle(sketch, "E98", {"center": v(-174.56, 257.77) * mm, "radius": 1.5 * mm});
            skCircle(sketch, "E99", {"center": v(-174.56, 212.77) * mm, "radius": 1.5 * mm});
            skCircle(sketch, "E100", {"center": v(-219.56, 212.77) * mm, "radius": 1.5 * mm});
            skPoint(sketch, "E101.visualSharp", {"position": v(-223.56, 261.77) * mm});
            skPoint(sketch, "E102.visualSharp", {"position": v(-170.56, 261.77) * mm});
            skPoint(sketch, "E103.visualSharp", {"position": v(-170.56, 208.77) * mm});
            skPoint(sketch, "E104.visualSharp", {"position": v(-223.56, 208.77) * mm});
            skPoint(sketch, "E105", {"position": v(-223.56, 235.27) * mm});
            skFitSpline(sketch, "E106", {"points": [v(-223.56, 261.77) * mm, v(-236.06, 235.27) * mm, v(-223.56, 208.77) * mm], "startDerivative": vector(-31.2, -16.8) * mm, "endDerivative": vector(31.2, -16.8) * mm});
            skCircle(sketch, "E107", {"center": v(-228.8, 235.27) * mm, "radius": 3.25 * mm});
            skArc(sketch, "E108.filletArc", {"start": v(-220.86, 261.77) * mm, "mid": v(-223.99, 261.14) * mm, "end": v(-226.61, 259.33) * mm});
            skArc(sketch, "E109.filletArc", {"start": v(-226.61, 211.21) * mm, "mid": v(-223.99, 209.4) * mm, "end": v(-220.86, 208.77) * mm});
            skLineSegment(sketch, "E110", {"start": v(-219.56, 212.77) * mm, "end": v(-174.56, 257.77) * mm});
            skLineSegment(sketch, "E111", {"start": v(-219.56, 257.77) * mm, "end": v(-174.56, 212.77) * mm});
            skPoint(sketch, "E112", {"position": v(-197.06, 235.27) * mm});
            skLineSegment(sketch, "E113", {"start": v(-197.06, 258.2) * mm, "end": v(-197.06, 212.74) * mm});
            skLineSegment(sketch, "E114", {"start": v(-217.73, 235.27) * mm, "end": v(-173.29, 235.27) * mm});
            skCircle(sketch, "E115", {"center": v(-189.63, 242.7) * mm, "radius": 1.5 * mm});
            skCircle(sketch, "E116", {"center": v(-184.68, 247.65) * mm, "radius": 1.5 * mm});
            skCircle(sketch, "E117", {"center": v(-186.56, 235.27) * mm, "radius": 1.5 * mm});
            skCircle(sketch, "E118", {"center": v(-179.56, 235.27) * mm, "radius": 1.5 * mm});
            skCircle(sketch, "E119", {"center": v(-197.06, 245.77) * mm, "radius": 1.5 * mm});
            skCircle(sketch, "E120", {"center": v(-197.06, 252.77) * mm, "radius": 1.5 * mm});
            skCircle(sketch, "E121", {"center": v(-209.43, 247.65) * mm, "radius": 1.5 * mm});
            skCircle(sketch, "E122", {"center": v(-204.48, 242.7) * mm, "radius": 1.5 * mm});
            skCircle(sketch, "E123", {"center": v(-207.56, 235.27) * mm, "radius": 1.5 * mm});
            skCircle(sketch, "E124", {"center": v(-214.56, 235.27) * mm, "radius": 1.5 * mm});
            skLineSegment(sketch, "E125", {"start": v(-198.56, 254.86) * mm, "end": v(-198.56, 241.57) * mm});
            skLineSegment(sketch, "E126", {"start": v(-195.56, 254.92) * mm, "end": v(-195.56, 241.46) * mm});
            skLineSegment(sketch, "E127", {"start": v(-177.05, 236.77) * mm, "end": v(-189.89, 236.77) * mm});
            skLineSegment(sketch, "E128", {"start": v(-189.77, 233.77) * mm, "end": v(-177.05, 233.77) * mm});
            skLineSegment(sketch, "E129", {"start": v(-205.04, 236.77) * mm, "end": v(-216.46, 236.77) * mm});
            skLineSegment(sketch, "E130", {"start": v(-217.02, 233.77) * mm, "end": v(-203.96, 233.77) * mm});
            skLineSegment(sketch, "E131", {"start": v(-212.56, 248.65) * mm, "end": v(-204.59, 240.68) * mm});
            skLineSegment(sketch, "E132", {"start": v(-209.94, 250.28) * mm, "end": v(-201.52, 241.85) * mm});
            skLineSegment(sketch, "E133", {"start": v(-184.71, 249.74) * mm, "end": v(-192.97, 241.49) * mm});
            skLineSegment(sketch, "E134", {"start": v(-181.54, 248.67) * mm, "end": v(-190.65, 239.56) * mm});
            skCircle(sketch, "E135.0.MirrorC", {"center": v(-209.43, 222.9) * mm, "radius": 1.5 * mm});
            skLineSegment(sketch, "E136.0.MirrorCS", {"start": v(-209.94, 220.27) * mm, "end": v(-201.52, 228.7) * mm});
            skLineSegment(sketch, "E137.0.MirrorCS", {"start": v(-212.56, 221.9) * mm, "end": v(-204.59, 229.86) * mm});
            skCircle(sketch, "E138.0.MirrorC", {"center": v(-204.48, 227.85) * mm, "radius": 1.5 * mm});
            skLineSegment(sketch, "E139.0.MirrorCS", {"start": v(-198.56, 215.68) * mm, "end": v(-198.56, 228.97) * mm});
            skCircle(sketch, "E140.0.MirrorC", {"center": v(-197.06, 224.77) * mm, "radius": 1.5 * mm});
            skLineSegment(sketch, "E141.0.MirrorCS", {"start": v(-195.56, 215.63) * mm, "end": v(-195.56, 229.08) * mm});
            skCircle(sketch, "E142.0.MirrorC", {"center": v(-197.06, 217.77) * mm, "radius": 1.5 * mm});
            skCircle(sketch, "E143.0.MirrorC", {"center": v(-189.63, 227.85) * mm, "radius": 1.5 * mm});
            skLineSegment(sketch, "E144.0.MirrorCS", {"start": v(-184.71, 220.8) * mm, "end": v(-192.97, 229.06) * mm});
            skCircle(sketch, "E145.0.MirrorC", {"center": v(-184.68, 222.9) * mm, "radius": 1.5 * mm});
            skLineSegment(sketch, "E146.0.MirrorCS", {"start": v(-181.54, 221.88) * mm, "end": v(-190.65, 230.98) * mm});
            skCircle(sketch, "E147", {"center": v(-197.06, 235.27) * mm, "radius": 1.5 * mm});
            skArc(sketch, "E148.0.MirrorCS", {"start": v(-173.25, 261.77) * mm, "mid": v(-170.13, 261.14) * mm, "end": v(-167.5, 259.33) * mm});
            skFitSpline(sketch, "E149.0.MirrorCS", {"points": [v(-170.56, 261.77) * mm, v(-158.06, 235.27) * mm, v(-170.56, 208.77) * mm], "startDerivative": vector(31.2, -16.8) * mm, "endDerivative": vector(-31.2, -16.8) * mm});
            skArc(sketch, "E150.0.MirrorCS", {"start": v(-167.5, 211.21) * mm, "mid": v(-170.13, 209.4) * mm, "end": v(-173.25, 208.77) * mm});
            skCircle(sketch, "E151.0.MirrorC", {"center": v(-165.3, 235.27) * mm, "radius": 3.25 * mm});
            skSolve(sketch);
        }
        {
            var Q0;
            Q0=makeQuery(id+"F49.imprint","IMPRINT",FACE,{"disambiguationData":[TD([[makeQuery(id+"F49.imprint","IMPRINT",EDGE,{"derivedFrom":sQuery(id+"F49.wireOp",EDGE,"E96.bottom")}),-1.0]])]});
            var Q1;
            {var subQ3=sQuery(id+"F49.wireOp",EDGE,"E106");Q1=makeQuery(id+"F49.imprint","IMPRINT",FACE,{"disambiguationData":[TD([[makeQuery(id+"F49.imprint","IMPRINT",EDGE,{"derivedFrom":subQ3}),1.0]])]});}
            extrude(context, id + "F50", {"entities" : qUnion([Q0, Q1]), "depth" : 1.8 * mm});
        }
    });
